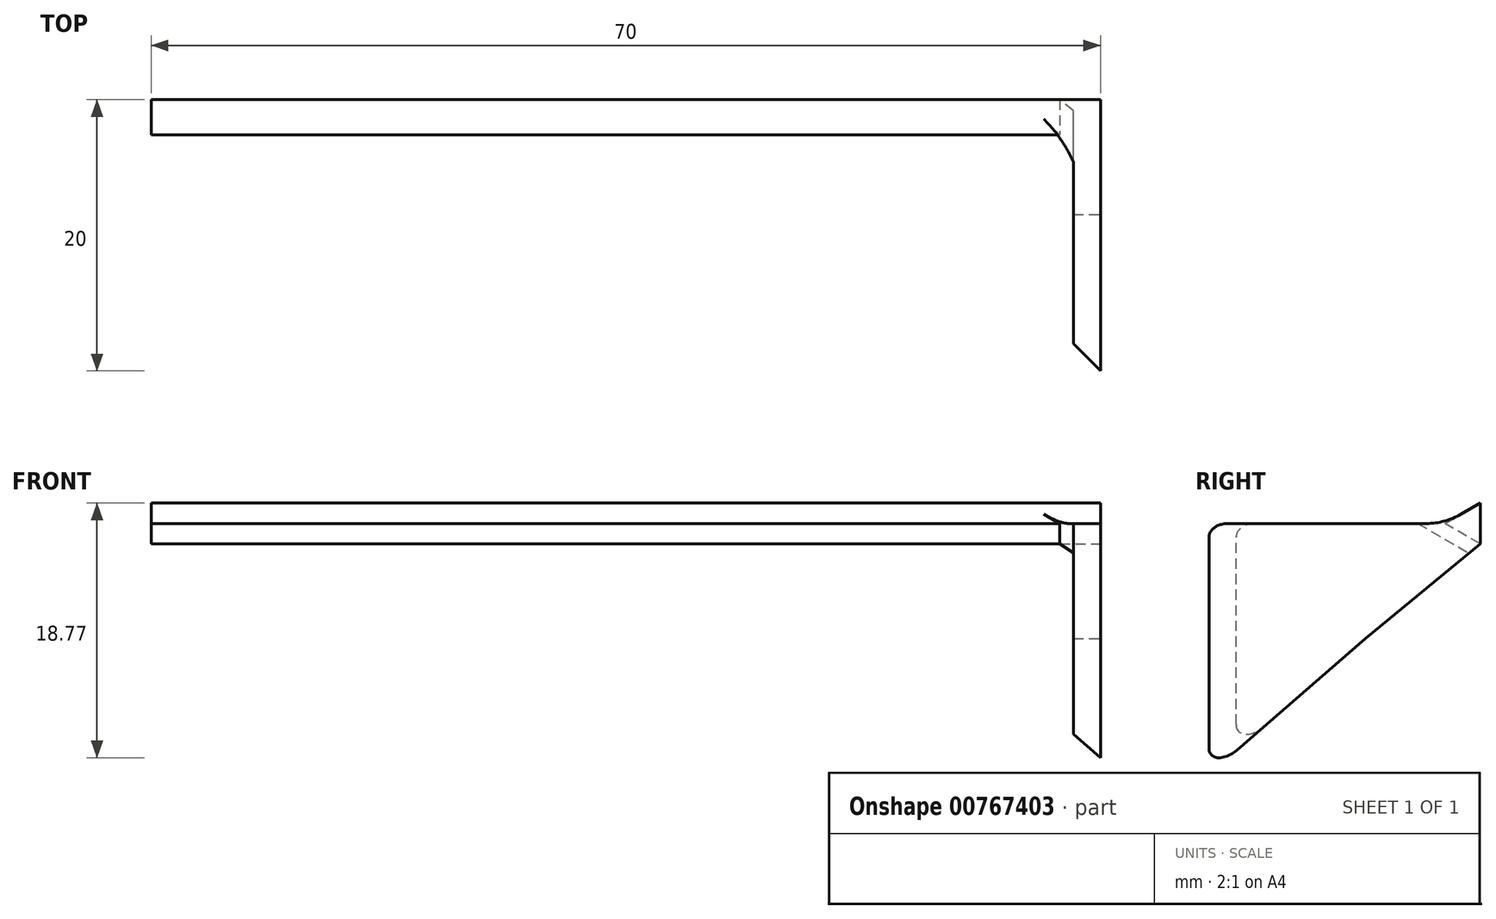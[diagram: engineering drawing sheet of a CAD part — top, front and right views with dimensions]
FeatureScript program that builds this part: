
annotation { "Feature Type Name" : "Feature", "Feature Type Description" : "" }
export const myFeature = defineFeature(function(context is Context, id is Id, definition is map)
    precondition{}
    {
        {
            var Q0;
            Q0=qCreatedBy(makeId("Right.planeOp"),FACE);
            var sketch = newSketch(context, id + "F0", { "sketchPlane" : qUnion([Q0])});
            skLineSegment(sketch, "E0.bottom", {"start": v(0, 0) * mm, "end": v(-10, 0) * mm});
            skLineSegment(sketch, "E0.top", {"start": v(0, -10) * mm, "end": v(-10, -10) * mm});
            skLineSegment(sketch, "E0.left", {"start": v(0, 0) * mm, "end": v(0, -10) * mm});
            skLineSegment(sketch, "E0.right", {"start": v(-10, 0) * mm, "end": v(-10, -10) * mm});
            skSolve(sketch);
        }
        {
            var Q0;
            Q0 = qSketchRegion(id + "F0", true);
            extrude(context, id + "F1", {"entities" : qUnion([Q0]), "depth" : 2 * mm, "offsetDistance" : 25.4 * mm});
        }
        {
            var Q0;
            Q0=makeQuery(id+"F1.opExtrude","CAP_FACE",FACE,{"disambiguationData":[OSD([sQuery(id+"F0.wireOp",EDGE,"E0.bottom"),sQuery(id+"F0.wireOp",EDGE,"E0.top"),sQuery(id+"F0.wireOp",EDGE,"E0.left"),sQuery(id+"F0.wireOp",EDGE,"E0.right")])],"isStart":false});
            var sketch = newSketch(context, id + "F2", { "sketchPlane" : qUnion([Q0])});
            skLineSegment(sketch, "E1", {"start": v(0, 0) * mm, "end": v(-2.6, -1.5) * mm});
            skLineSegment(sketch, "E2", {"start": v(-2.6, -1.5) * mm, "end": v(0, -3) * mm});
            skLineSegment(sketch, "E3", {"start": v(0, -3) * mm, "end": v(0, 0) * mm});
            skSolve(sketch);
        }
        {
            var Q0;
            Q0 = qSketchRegion(id + "F2", true);
            extrude(context, id + "F3", {"entities" : qUnion([Q0]), "operationType" : NewBodyOperationType.ADD, "oppositeDirection" : true, "depth" : 60 * mm, "offsetDistance" : 25.4 * mm});
        }
        {
            var Q0;
            Q0=makeQuery(id+"F1.opExtrude","CAP_FACE",FACE,{"disambiguationData":[OSD([sQuery(id+"F0.wireOp",EDGE,"E0.bottom"),sQuery(id+"F0.wireOp",EDGE,"E0.top"),sQuery(id+"F0.wireOp",EDGE,"E0.left"),sQuery(id+"F0.wireOp",EDGE,"E0.right")])],"isStart":true});
            var sketch = newSketch(context, id + "F4", { "sketchPlane" : qUnion([Q0])});
            skLineSegment(sketch, "E4", {"start": v(0, 0) * mm, "end": v(2.6, -1.5) * mm});
            skLineSegment(sketch, "E5", {"start": v(2.6, -1.5) * mm, "end": v(10, 0) * mm});
            skLineSegment(sketch, "E6", {"start": v(10, 0) * mm, "end": v(0, 0) * mm});
            skSolve(sketch);
        }
        {
            var Q0;
            Q0 = qSketchRegion(id + "F4", true);
            extrude(context, id + "F5", {"entities" : qUnion([Q0]), "operationType" : NewBodyOperationType.REMOVE, "endBound" : BoundingType.UP_TO_NEXT, "oppositeDirection" : true, "depth" : 25.4 * mm, "offsetDistance" : 25.4 * mm});
        }
        {
            var Q0;
            Q0=makeQuery(id+"F1.opExtrude","CAP_FACE",FACE,{"disambiguationData":[OSD([sQuery(id+"F0.wireOp",EDGE,"E0.bottom"),sQuery(id+"F0.wireOp",EDGE,"E0.top"),sQuery(id+"F0.wireOp",EDGE,"E0.left"),sQuery(id+"F0.wireOp",EDGE,"E0.right")])],"isStart":false});
            var sketch = newSketch(context, id + "F6", { "sketchPlane" : qUnion([Q0])});
            skLineSegment(sketch, "E7", {"start": v(-2.6, -1.5) * mm, "end": v(-10, -1.5) * mm});
            skLineSegment(sketch, "E8", {"start": v(-10, -1.5) * mm, "end": v(-10, 0) * mm});
            skLineSegment(sketch, "E9", {"start": v(-10, 0) * mm, "end": v(-2.6, -1.5) * mm});
            skSolve(sketch);
        }
        {
            var Q0;
            Q0 = qSketchRegion(id + "F6", true);
            extrude(context, id + "F7", {"entities" : qUnion([Q0]), "operationType" : NewBodyOperationType.REMOVE, "endBound" : BoundingType.UP_TO_NEXT, "oppositeDirection" : true, "depth" : 25.4 * mm, "offsetDistance" : 25.4 * mm});
        }
        {
            var Q0;
            Q0=makeQuery(id+"F1.opExtrude","CAP_FACE",FACE,{"disambiguationData":[OSD([sQuery(id+"F0.wireOp",EDGE,"E0.bottom"),sQuery(id+"F0.wireOp",EDGE,"E0.top"),sQuery(id+"F0.wireOp",EDGE,"E0.left"),sQuery(id+"F0.wireOp",EDGE,"E0.right")])],"isStart":false});
            var sketch = newSketch(context, id + "F8", { "sketchPlane" : qUnion([Q0])});
            skLineSegment(sketch, "E10", {"start": v(0, -3.01) * mm, "end": v(-8.47, -10) * mm});
            skLineSegment(sketch, "E11", {"start": v(-8.47, -10) * mm, "end": v(-10, -8.14) * mm});
            skLineSegment(sketch, "E12", {"start": v(-10, -8.14) * mm, "end": v(-10, -10) * mm});
            skLineSegment(sketch, "E13", {"start": v(-10, -10) * mm, "end": v(-8.47, -10) * mm});
            skLineSegment(sketch, "E14", {"start": v(0, -10) * mm, "end": v(0, -3.01) * mm});
            skLineSegment(sketch, "E15", {"start": v(-8.47, -10) * mm, "end": v(0, -10) * mm});
            skSolve(sketch);
        }
        {
            var Q0;
            Q0=makeQuery(id+"F3.boolean.opBoolean","INTERSECT",EDGE,{"derivedFrom":[makeQuery(id+"F1.opExtrude","CAP_FACE",FACE,{"disambiguationData":[OSD([sQuery(id+"F0.wireOp",EDGE,"E0.bottom"),sQuery(id+"F0.wireOp",EDGE,"E0.top"),sQuery(id+"F0.wireOp",EDGE,"E0.left"),sQuery(id+"F0.wireOp",EDGE,"E0.right")])],"isStart":true}),makeQuery(id+"F3.opExtrude","SWEPT_FACE",FACE,{"disambiguationData":[OSD([sQuery(id+"F2.wireOp",EDGE,"E2")])]})]});
            chamfer(context, id + "F9", {"entities" : qUnion([Q0]), "width" : 1 * mm, "tangentPropagation" : true});
        }
        {
            var Q0;
            {var subQ0=sQuery(id+"F4.wireOp",EDGE,"E5");var subQ1=sQuery(id+"F4.wireOp",EDGE,"E4");var subQ2=sQuery(id+"F2.wireOp",EDGE,"E2");var subQ3=sQuery(id+"F2.wireOp",EDGE,"E1");var subQ4=sQuery(id+"F0.wireOp",EDGE,"E0.right");var subQ5=sQuery(id+"F0.wireOp",EDGE,"E0.left");var subQ6=sQuery(id+"F0.wireOp",EDGE,"E0.top");var subQ7=sQuery(id+"F0.wireOp",EDGE,"E0.bottom");Q0=makeQuery(id+"F7.boolean.opBoolean","MERGE",EDGE,{"derivedFrom":[makeQuery(id+"F5.boolean.opBoolean","COPY",EDGE,{"derivedFrom":makeQuery(id+"F5.opExtrude","SWEPT_EDGE",EDGE,{"disambiguationData":[OSD([subQ7,subQ6,subQ5,subQ4,subQ3,subQ2,subQ1,subQ0])]})}),makeQuery(id+"F7.opExtrude","SWEPT_EDGE",EDGE,{"disambiguationData":[OSD([subQ7,subQ6,subQ5,subQ4,subQ3,subQ2,subQ1,subQ0,sQuery(id+"F6.wireOp",EDGE,"E7"),sQuery(id+"F6.wireOp",EDGE,"E9")])]})]});}
            fillet(context, id + "F10", {"entities" : qUnion([Q0]), "radius" : 5.08 * mm, "tangentPropagation" : true, "allowEdgeOverflow" : false});
        }
        {
            var Q0;
            Q0=makeQuery(id+"F8.imprint","IMPRINT",FACE,{"disambiguationData":[TD([[makeQuery(id+"F8.imprint","IMPRINT",EDGE,{"derivedFrom":sQuery(id+"F8.wireOp",EDGE,"E10")}),1.0]])]});
            extrude(context, id + "F11", {"entities" : qUnion([Q0]), "operationType" : NewBodyOperationType.REMOVE, "endBound" : BoundingType.UP_TO_NEXT, "oppositeDirection" : true, "depth" : 25.4 * mm, "offsetDistance" : 25.4 * mm});
        }
        {
            var Q0;
            Q0=makeQuery(id+"F3.opExtrude","CAP_FACE",FACE,{"disambiguationData":[OSD([sQuery(id+"F2.wireOp",EDGE,"E1"),sQuery(id+"F2.wireOp",EDGE,"E2"),sQuery(id+"F2.wireOp",EDGE,"E3")])],"isStart":false});
            extrude(context, id + "F12", {"entities" : qUnion([Q0]), "operationType" : NewBodyOperationType.ADD, "depth" : 10 * mm, "offsetDistance" : 25.4 * mm});
        }
        {
            var Q0;
            Q0=makeQuery(id+"F1.opExtrude","SWEPT_FACE",FACE,{"disambiguationData":[OSD([sQuery(id+"F0.wireOp",EDGE,"E0.right")])]});
            extrude(context, id + "F13", {"entities" : qUnion([Q0]), "operationType" : NewBodyOperationType.ADD, "depth" : 10 * mm, "offsetDistance" : 25.4 * mm});
        }
        {
            var Q0;
            {var subQ0=sQuery(id+"F0.wireOp",EDGE,"E0.top");Q0=makeQuery(id+"F13.boolean.opBoolean","MERGE",FACE,{"derivedFrom":[makeQuery(id+"F1.opExtrude","SWEPT_FACE",FACE,{"disambiguationData":[OSD([subQ0])]}),makeQuery(id+"F13.opExtrude","SWEPT_FACE",FACE,{"disambiguationData":[OSD([subQ0,sQuery(id+"F0.wireOp",EDGE,"E0.right")])]})]});}
            extrude(context, id + "F14", {"entities" : qUnion([Q0]), "operationType" : NewBodyOperationType.ADD, "depth" : 10 * mm, "offsetDistance" : 25.4 * mm});
        }
        {
            var Q0;
            {var subQ0=sQuery(id+"F0.wireOp",EDGE,"E0.right");var subQ1=sQuery(id+"F0.wireOp",EDGE,"E0.top");Q0=makeQuery(id+"F14.boolean.opBoolean","MERGE",FACE,{"derivedFrom":[makeQuery(id+"F13.boolean.opBoolean","MERGE",FACE,{"derivedFrom":[makeQuery(id+"F1.opExtrude","CAP_FACE",FACE,{"disambiguationData":[OSD([sQuery(id+"F0.wireOp",EDGE,"E0.bottom"),subQ1,sQuery(id+"F0.wireOp",EDGE,"E0.left"),subQ0])],"isStart":false}),makeQuery(id+"F13.opExtrude","SWEPT_FACE",FACE,{"disambiguationData":[OSD([subQ0]),TDD([makeQuery(id+"F1.opExtrude","CAP_EDGE",EDGE,{"disambiguationData":[OSD([subQ0])],"isStart":false})])]})]}),makeQuery(id+"F14.opExtrude","SWEPT_FACE",FACE,{"disambiguationData":[OSD([subQ1,subQ0]),TDD([makeQuery(id+"F13.boolean.opBoolean","MERGE",EDGE,{"derivedFrom":[makeQuery(id+"F1.opExtrude","CAP_EDGE",EDGE,{"disambiguationData":[OSD([subQ1])],"isStart":false}),makeQuery(id+"F13.opExtrude","SWEPT_EDGE",EDGE,{"disambiguationData":[OSD([subQ1,subQ0]),TDD([makeQuery(id+"F1.opExtrude","CAP_VERTEX",VERTEX,{"disambiguationData":[OSD([subQ1,subQ0])],"isStart":false})])]})]})])]})]});}
            var sketch = newSketch(context, id + "F15", { "sketchPlane" : qUnion([Q0])});
            skLineSegment(sketch, "E16", {"start": v(-8.47, -10) * mm, "end": v(-20, -20) * mm});
            skLineSegment(sketch, "E17", {"start": v(-20, -20) * mm, "end": v(-8.47, -20) * mm});
            skLineSegment(sketch, "E18", {"start": v(-8.47, -20) * mm, "end": v(-8.47, -10) * mm});
            skSolve(sketch);
        }
        {
            var Q0;
            Q0 = qSketchRegion(id + "F15", true);
            extrude(context, id + "F16", {"entities" : qUnion([Q0]), "operationType" : NewBodyOperationType.REMOVE, "endBound" : BoundingType.UP_TO_NEXT, "oppositeDirection" : true, "depth" : 25.4 * mm, "offsetDistance" : 25.4 * mm});
        }
        {
            var Q0;
            {var subQ0=sQuery(id+"F0.wireOp",EDGE,"E0.right");var subQ1=sQuery(id+"F0.wireOp",EDGE,"E0.top");Q0=makeQuery(id+"F14.boolean.opBoolean","MERGE",EDGE,{"derivedFrom":[makeQuery(id+"F13.opExtrude","CAP_EDGE",EDGE,{"disambiguationData":[OSD([subQ0]),TDD([makeQuery(id+"F1.opExtrude","CAP_EDGE",EDGE,{"disambiguationData":[OSD([subQ0])],"isStart":true})])],"isStart":false}),makeQuery(id+"F14.opExtrude","SWEPT_EDGE",EDGE,{"disambiguationData":[OSD([subQ1,subQ0]),TDD([makeQuery(id+"F13.opExtrude","CAP_VERTEX",VERTEX,{"disambiguationData":[OSD([subQ1,subQ0]),TDD([makeQuery(id+"F1.opExtrude","CAP_VERTEX",VERTEX,{"disambiguationData":[OSD([subQ1,subQ0])],"isStart":true})])],"isStart":false})])]})]});}
            chamfer(context, id + "F17", {"entities" : qUnion([Q0]), "width" : 2 * mm, "tangentPropagation" : true});
        }
        {
            var Q0;
            {var subQ0=sQuery(id+"F6.wireOp",EDGE,"E7");var subQ1=sQuery(id+"F0.wireOp",EDGE,"E0.right");var subQ2=sQuery(id+"F0.wireOp",EDGE,"E0.top");Q0=makeQuery(id+"F17.opChamfer","BLEND_EDGE",EDGE,{"blendedFrom":[makeQuery(id+"F14.boolean.opBoolean","MERGE",EDGE,{"derivedFrom":[makeQuery(id+"F13.opExtrude","CAP_EDGE",EDGE,{"disambiguationData":[OSD([subQ1]),TDD([makeQuery(id+"F1.opExtrude","CAP_EDGE",EDGE,{"disambiguationData":[OSD([subQ1])],"isStart":true})])],"isStart":false}),makeQuery(id+"F14.opExtrude","SWEPT_EDGE",EDGE,{"disambiguationData":[OSD([subQ2,subQ1]),TDD([makeQuery(id+"F13.opExtrude","CAP_VERTEX",VERTEX,{"disambiguationData":[OSD([subQ2,subQ1]),TDD([makeQuery(id+"F1.opExtrude","CAP_VERTEX",VERTEX,{"disambiguationData":[OSD([subQ2,subQ1])],"isStart":true})])],"isStart":false})])]})]}),makeQuery(id+"F13.boolean.opBoolean","MERGE",FACE,{"derivedFrom":[makeQuery(id+"F7.boolean.opBoolean","COPY",FACE,{"derivedFrom":makeQuery(id+"F7.opExtrude","SWEPT_FACE",FACE,{"disambiguationData":[OSD([subQ0])]})}),makeQuery(id+"F13.opExtrude","SWEPT_FACE",FACE,{"disambiguationData":[OSD([subQ1,subQ0,sQuery(id+"F6.wireOp",EDGE,"E8")])]})]})],"blendedInto":[makeQuery(id+"F13.boolean.opBoolean","MERGE",FACE,{"derivedFrom":[makeQuery(id+"F7.boolean.opBoolean","COPY",FACE,{"derivedFrom":makeQuery(id+"F7.opExtrude","SWEPT_FACE",FACE,{"disambiguationData":[OSD([subQ0])]})}),makeQuery(id+"F13.opExtrude","SWEPT_FACE",FACE,{"disambiguationData":[OSD([subQ1,subQ0,sQuery(id+"F6.wireOp",EDGE,"E8")])]})]})]});}
            var Q1;
            {var subQ0=sQuery(id+"F0.wireOp",EDGE,"E0.right");var subQ1=sQuery(id+"F0.wireOp",EDGE,"E0.top");Q1=makeQuery(id+"F17.opChamfer","BLEND_EDGE",EDGE,{"blendedFrom":[makeQuery(id+"F14.boolean.opBoolean","MERGE",EDGE,{"derivedFrom":[makeQuery(id+"F13.opExtrude","CAP_EDGE",EDGE,{"disambiguationData":[OSD([subQ0]),TDD([makeQuery(id+"F1.opExtrude","CAP_EDGE",EDGE,{"disambiguationData":[OSD([subQ0])],"isStart":true})])],"isStart":false}),makeQuery(id+"F14.opExtrude","SWEPT_EDGE",EDGE,{"disambiguationData":[OSD([subQ1,subQ0]),TDD([makeQuery(id+"F13.opExtrude","CAP_VERTEX",VERTEX,{"disambiguationData":[OSD([subQ1,subQ0]),TDD([makeQuery(id+"F1.opExtrude","CAP_VERTEX",VERTEX,{"disambiguationData":[OSD([subQ1,subQ0])],"isStart":true})])],"isStart":false})])]})]}),makeQuery(id+"F16.boolean.opBoolean","COPY",FACE,{"derivedFrom":makeQuery(id+"F16.opExtrude","SWEPT_FACE",FACE,{"disambiguationData":[OSD([sQuery(id+"F15.wireOp",EDGE,"E16")])]})})],"blendedInto":[makeQuery(id+"F16.boolean.opBoolean","COPY",FACE,{"derivedFrom":makeQuery(id+"F16.opExtrude","SWEPT_FACE",FACE,{"disambiguationData":[OSD([sQuery(id+"F15.wireOp",EDGE,"E16")])]})})]});}
            fillet(context, id + "F18", {"entities" : qUnion([Q0, Q1]), "radius" : 1 * mm, "tangentPropagation" : true, "allowEdgeOverflow" : false});
        }
    });
